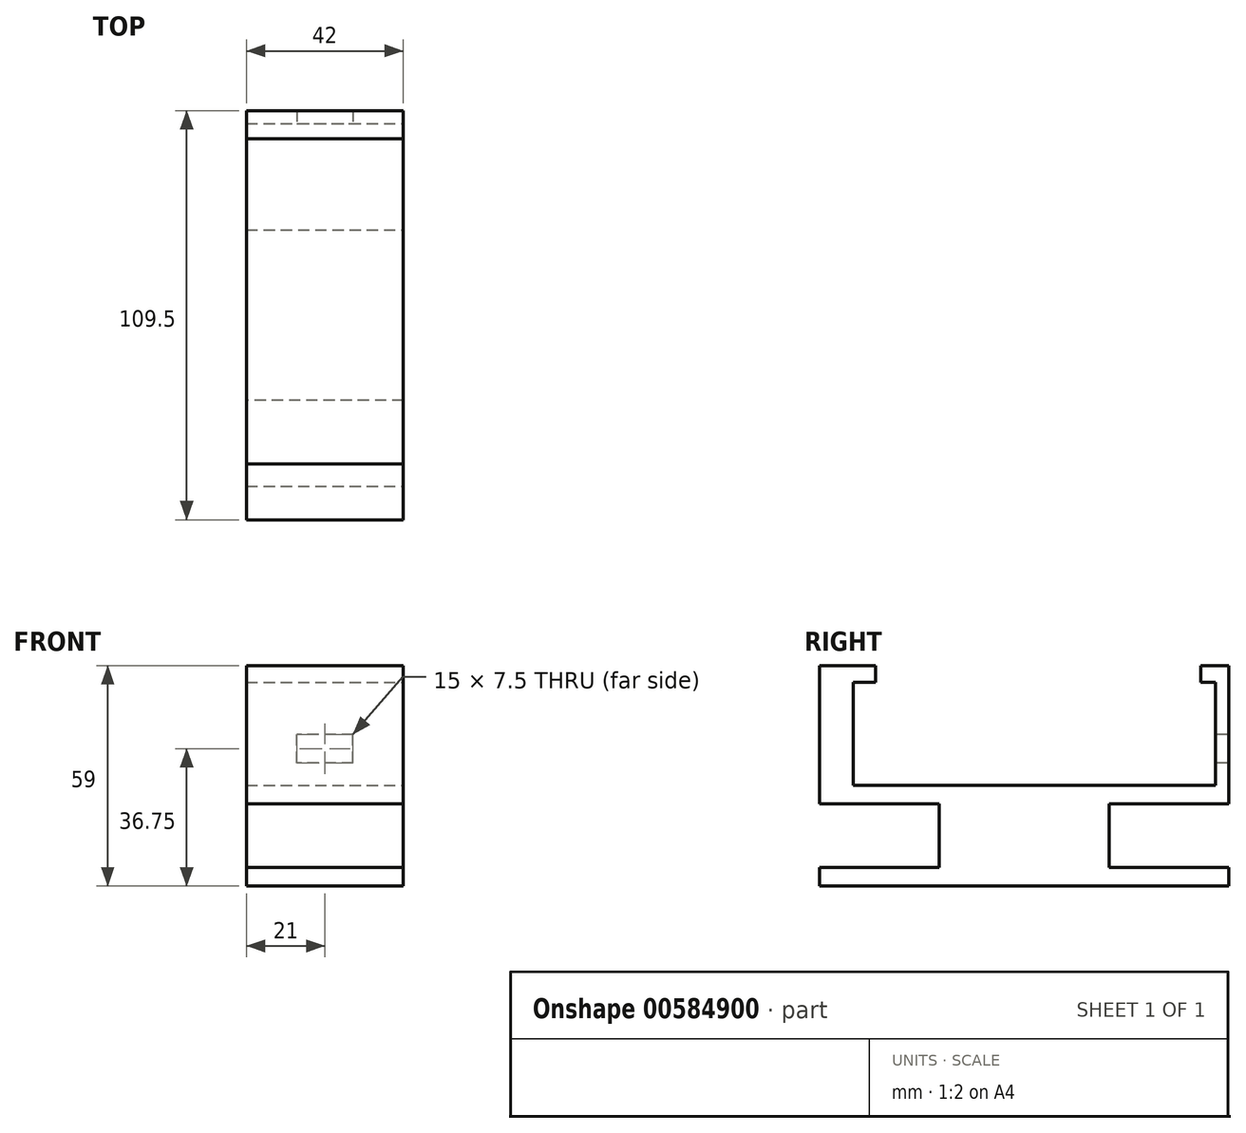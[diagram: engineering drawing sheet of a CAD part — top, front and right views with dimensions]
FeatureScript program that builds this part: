
annotation { "Feature Type Name" : "Feature", "Feature Type Description" : "" }
export const myFeature = defineFeature(function(context is Context, id is Id, definition is map)
    precondition{}
    {
        {
            var Q0;
            Q0=qCreatedBy(makeId("Top.planeOp"),FACE);
            var sketch = newSketch(context, id + "F0", { "sketchPlane" : qUnion([Q0])});
            skLineSegment(sketch, "E0.bottom", {"start": v(-21, 54.75) * mm, "end": v(21, 54.75) * mm});
            skLineSegment(sketch, "E0.top", {"start": v(-21, -54.75) * mm, "end": v(21, -54.75) * mm});
            skLineSegment(sketch, "E0.left", {"start": v(-21, 54.75) * mm, "end": v(-21, -54.75) * mm});
            skLineSegment(sketch, "E0.right", {"start": v(21, 54.75) * mm, "end": v(21, -54.75) * mm});
            skPoint(sketch, "E0.middle", {"position": v(0, 0) * mm});
            skSolve(sketch);
        }
        {
            var Q0;
            Q0=makeQuery(id+"F0.imprint","IMPRINT",FACE,{"disambiguationData":[TD([[makeQuery(id+"F0.imprint","IMPRINT",EDGE,{"derivedFrom":sQuery(id+"F0.wireOp",EDGE,"E0.bottom")}),-1.0]])]});
            extrude(context, id + "F1", {"entities" : qUnion([Q0]), "depth" : 5 * mm, "offsetDistance" : 25 * mm});
        }
        {
            var Q0;
            Q0=makeQuery(id+"F1.opExtrude","CAP_FACE",FACE,{"disambiguationData":[OSD([sQuery(id+"F0.wireOp",EDGE,"E0.bottom"),sQuery(id+"F0.wireOp",EDGE,"E0.top"),sQuery(id+"F0.wireOp",EDGE,"E0.left"),sQuery(id+"F0.wireOp",EDGE,"E0.right")])],"isStart":false});
            var sketch = newSketch(context, id + "F2", { "sketchPlane" : qUnion([Q0])});
            skLineSegment(sketch, "E1.bottom", {"start": v(-21, 54.75) * mm, "end": v(21, 54.75) * mm});
            skLineSegment(sketch, "E1.top", {"start": v(-21, 47.25) * mm, "end": v(21, 47.25) * mm});
            skLineSegment(sketch, "E1.left", {"start": v(-21, 54.75) * mm, "end": v(-21, 47.25) * mm});
            skLineSegment(sketch, "E1.right", {"start": v(21, 54.75) * mm, "end": v(21, 47.25) * mm});
            skPoint(sketch, "E1.middle", {"position": v(0, 51) * mm});
            skLineSegment(sketch, "E2.bottom", {"start": v(-21, -39.75) * mm, "end": v(21, -39.75) * mm});
            skLineSegment(sketch, "E2.top", {"start": v(-21, -54.75) * mm, "end": v(21, -54.75) * mm});
            skLineSegment(sketch, "E2.left", {"start": v(-21, -39.75) * mm, "end": v(-21, -54.75) * mm});
            skLineSegment(sketch, "E2.right", {"start": v(21, -39.75) * mm, "end": v(21, -54.75) * mm});
            skPoint(sketch, "E2.middle", {"position": v(0, -47.25) * mm});
            skSolve(sketch);
        }
        {
            var Q0;
            Q0=makeQuery(id+"F2.imprint","IMPRINT",FACE,{"disambiguationData":[TD([[makeQuery(id+"F2.imprint","IMPRINT",EDGE,{"derivedFrom":sQuery(id+"F2.wireOp",EDGE,"gTRGSuqZ-lPxv-xSsv-gjWA-rCe4dbmy2frY.bottom")}),-1.0]])]});
            var Q1;
            Q1=makeQuery(id+"F2.imprint","IMPRINT",FACE,{"disambiguationData":[TD([[makeQuery(id+"F2.imprint","IMPRINT",EDGE,{"derivedFrom":sQuery(id+"F2.wireOp",EDGE,"5NfKlNX9-xNwy-tjNF-5iGd-XRvzVmTsgCSR.bottom")}),1.0]])]});
            var Q2;
            Q2=makeQuery(id+"F2.imprint","IMPRINT",FACE,{"disambiguationData":[TD([[makeQuery(id+"F2.imprint","IMPRINT",EDGE,{"derivedFrom":sQuery(id+"F2.wireOp",EDGE,"E1.bottom")}),-1.0]])]});
            var Q3;
            Q3=makeQuery(id+"F2.imprint","IMPRINT",FACE,{"disambiguationData":[TD([[makeQuery(id+"F2.imprint","IMPRINT",EDGE,{"derivedFrom":sQuery(id+"F2.wireOp",EDGE,"E2.bottom")}),-1.0]])]});
            extrude(context, id + "F3", {"entities" : qUnion([Q0, Q1, Q2, Q3]), "operationType" : NewBodyOperationType.ADD, "depth" : 32 * mm, "offsetDistance" : 25 * mm});
        }
        {
            var Q0;
            Q0=makeQuery(id+"F3.opExtrude","SWEPT_FACE",FACE,{"disambiguationData":[OSD([sQuery(id+"F2.wireOp",EDGE,"E1.top")])]});
            var sketch = newSketch(context, id + "F4", { "sketchPlane" : qUnion([Q0])});
            skLineSegment(sketch, "E3.bottom", {"start": v(-21, 32.5) * mm, "end": v(21, 32.5) * mm});
            skLineSegment(sketch, "E3.top", {"start": v(-21, 5) * mm, "end": v(21, 5) * mm});
            skLineSegment(sketch, "E3.left", {"start": v(-21, 32.5) * mm, "end": v(-21, 5) * mm});
            skLineSegment(sketch, "E3.right", {"start": v(21, 32.5) * mm, "end": v(21, 5) * mm});
            skSolve(sketch);
        }
        {
            var Q0;
            Q0=makeQuery(id+"F4.imprint","IMPRINT",FACE,{"disambiguationData":[TD([[makeQuery(id+"F4.imprint","IMPRINT",EDGE,{"derivedFrom":sQuery(id+"F4.wireOp",EDGE,"E3.bottom")}),-1.0]])]});
            extrude(context, id + "F5", {"entities" : qUnion([Q0]), "operationType" : NewBodyOperationType.REMOVE, "oppositeDirection" : true, "depth" : 4 * mm, "offsetDistance" : 25 * mm});
        }
        {
            var Q0;
            Q0=makeQuery(id+"F3.opExtrude","SWEPT_FACE",FACE,{"disambiguationData":[OSD([sQuery(id+"F2.wireOp",EDGE,"E2.bottom")])]});
            var sketch = newSketch(context, id + "F6", { "sketchPlane" : qUnion([Q0])});
            skLineSegment(sketch, "E4.bottom", {"start": v(-21, 32.5) * mm, "end": v(21, 32.5) * mm});
            skLineSegment(sketch, "E4.top", {"start": v(-21, 5) * mm, "end": v(21, 5) * mm});
            skLineSegment(sketch, "E4.left", {"start": v(-21, 32.5) * mm, "end": v(-21, 5) * mm});
            skLineSegment(sketch, "E4.right", {"start": v(21, 32.5) * mm, "end": v(21, 5) * mm});
            skSolve(sketch);
        }
        {
            var Q0;
            Q0=makeQuery(id+"F6.imprint","IMPRINT",FACE,{"disambiguationData":[TD([[makeQuery(id+"F6.imprint","IMPRINT",EDGE,{"derivedFrom":sQuery(id+"F6.wireOp",EDGE,"E4.bottom")}),-1.0]])]});
            extrude(context, id + "F7", {"entities" : qUnion([Q0]), "operationType" : NewBodyOperationType.REMOVE, "oppositeDirection" : true, "depth" : 6 * mm, "offsetDistance" : 25 * mm});
        }
        {
            var Q0;
            Q0=makeQuery(id+"F5.boolean.opBoolean","COPY",FACE,{"derivedFrom":makeQuery(id+"F5.opExtrude","CAP_FACE",FACE,{"disambiguationData":[OSD([sQuery(id+"F4.wireOp",EDGE,"E3.bottom"),sQuery(id+"F4.wireOp",EDGE,"E3.top"),sQuery(id+"F4.wireOp",EDGE,"E3.left"),sQuery(id+"F4.wireOp",EDGE,"E3.right")])],"isStart":false})});
            var sketch = newSketch(context, id + "F8", { "sketchPlane" : qUnion([Q0])});
            skLineSegment(sketch, "E5.bottom", {"start": v(-7.5, 18.5) * mm, "end": v(7.5, 18.5) * mm});
            skLineSegment(sketch, "E5.top", {"start": v(-7.5, 11) * mm, "end": v(7.5, 11) * mm});
            skLineSegment(sketch, "E5.left", {"start": v(-7.5, 18.5) * mm, "end": v(-7.5, 11) * mm});
            skLineSegment(sketch, "E5.right", {"start": v(7.5, 18.5) * mm, "end": v(7.5, 11) * mm});
            skPoint(sketch, "E5.middle", {"position": v(0, 14.75) * mm});
            skSolve(sketch);
        }
        {
            var Q0;
            Q0=makeQuery(id+"F8.imprint","IMPRINT",FACE,{"disambiguationData":[TD([[makeQuery(id+"F8.imprint","IMPRINT",EDGE,{"derivedFrom":sQuery(id+"F8.wireOp",EDGE,"E5.bottom")}),-1.0]])]});
            extrude(context, id + "F9", {"entities" : qUnion([Q0]), "operationType" : NewBodyOperationType.REMOVE, "endBound" : BoundingType.THROUGH_ALL, "oppositeDirection" : true, "depth" : 25 * mm, "offsetDistance" : 25 * mm});
        }
        {
            var Q0;
            Q0=makeQuery(id+"F1.opExtrude","CAP_FACE",FACE,{"disambiguationData":[OSD([sQuery(id+"F0.wireOp",EDGE,"E0.bottom"),sQuery(id+"F0.wireOp",EDGE,"E0.top"),sQuery(id+"F0.wireOp",EDGE,"E0.left"),sQuery(id+"F0.wireOp",EDGE,"E0.right")])],"isStart":true});
            var sketch = newSketch(context, id + "F10", { "sketchPlane" : qUnion([Q0])});
            skLineSegment(sketch, "E6.bottom", {"start": v(-21, -54.75) * mm, "end": v(21, -54.75) * mm});
            skLineSegment(sketch, "E6.top", {"start": v(-21, 0) * mm, "end": v(21, 0) * mm});
            skLineSegment(sketch, "E6.left", {"start": v(-21, -54.75) * mm, "end": v(-21, 0) * mm});
            skLineSegment(sketch, "E6.right", {"start": v(21, -54.75) * mm, "end": v(21, 0) * mm});
            skLineSegment(sketch, "E7.bottom", {"start": v(-21, 54.75) * mm, "end": v(21, 54.75) * mm});
            skLineSegment(sketch, "E7.left", {"start": v(-21, 54.75) * mm, "end": v(-21, 0) * mm});
            skLineSegment(sketch, "E7.right", {"start": v(21, 54.75) * mm, "end": v(21, 0) * mm});
            skSolve(sketch);
        }
        {
            var Q0;
            Q0=qSketchRegion(id+"F10",true);
            extrude(context, id + "F11", {"entities" : qUnion([Q0]), "operationType" : NewBodyOperationType.ADD, "depth" : 22 * mm, "offsetDistance" : 25 * mm});
        }
        {
            var Q0;
            Q0=makeQuery(id+"F11.boolean.opBoolean","MERGE",FACE,{"derivedFrom":[makeQuery(id+"F3.boolean.opBoolean","MERGE",FACE,{"derivedFrom":[makeQuery(id+"F1.opExtrude","SWEPT_FACE",FACE,{"disambiguationData":[OSD([sQuery(id+"F0.wireOp",EDGE,"E0.bottom")])]}),makeQuery(id+"F3.opExtrude","SWEPT_FACE",FACE,{"disambiguationData":[OSD([sQuery(id+"F2.wireOp",EDGE,"E1.bottom")])]})]}),makeQuery(id+"F11.opExtrude","SWEPT_FACE",FACE,{"disambiguationData":[OSD([sQuery(id+"F10.wireOp",EDGE,"E6.bottom")])]})]});
            var sketch = newSketch(context, id + "F12", { "sketchPlane" : qUnion([Q0])});
            skLineSegment(sketch, "E8.bottom", {"start": v(21, -17) * mm, "end": v(-21, -17) * mm});
            skLineSegment(sketch, "E8.top", {"start": v(21, 0) * mm, "end": v(-21, 0) * mm});
            skLineSegment(sketch, "E8.left", {"start": v(21, -17) * mm, "end": v(21, 0) * mm});
            skLineSegment(sketch, "E8.right", {"start": v(-21, -17) * mm, "end": v(-21, 0) * mm});
            skSolve(sketch);
        }
        {
            var Q0;
            Q0=makeQuery(id+"F12.imprint","IMPRINT",FACE,{"disambiguationData":[TD([[makeQuery(id+"F12.imprint","IMPRINT",EDGE,{"derivedFrom":sQuery(id+"F12.wireOp",EDGE,"E8.bottom")}),-1.0]])]});
            extrude(context, id + "F13", {"entities" : qUnion([Q0]), "operationType" : NewBodyOperationType.REMOVE, "oppositeDirection" : true, "depth" : 32 * mm, "offsetDistance" : 25 * mm});
        }
        {
            var Q0;
            Q0=makeQuery(id+"F11.boolean.opBoolean","MERGE",FACE,{"derivedFrom":[makeQuery(id+"F3.boolean.opBoolean","MERGE",FACE,{"derivedFrom":[makeQuery(id+"F1.opExtrude","SWEPT_FACE",FACE,{"disambiguationData":[OSD([sQuery(id+"F0.wireOp",EDGE,"E0.top")])]}),makeQuery(id+"F3.opExtrude","SWEPT_FACE",FACE,{"disambiguationData":[OSD([sQuery(id+"F2.wireOp",EDGE,"E2.top")])]})]}),makeQuery(id+"F11.opExtrude","SWEPT_FACE",FACE,{"disambiguationData":[OSD([sQuery(id+"F10.wireOp",EDGE,"E7.bottom")])]})]});
            var sketch = newSketch(context, id + "F14", { "sketchPlane" : qUnion([Q0])});
            skLineSegment(sketch, "E9.bottom", {"start": v(21, -17) * mm, "end": v(-21, -17) * mm});
            skLineSegment(sketch, "E9.top", {"start": v(21, 0) * mm, "end": v(-21, 0) * mm});
            skLineSegment(sketch, "E9.left", {"start": v(21, -17) * mm, "end": v(21, 0) * mm});
            skLineSegment(sketch, "E9.right", {"start": v(-21, -17) * mm, "end": v(-21, 0) * mm});
            skSolve(sketch);
        }
        {
            var Q0;
            Q0=makeQuery(id+"F14.imprint","IMPRINT",FACE,{"disambiguationData":[TD([[makeQuery(id+"F14.imprint","IMPRINT",EDGE,{"derivedFrom":sQuery(id+"F14.wireOp",EDGE,"E9.bottom")}),-1.0]])]});
            extrude(context, id + "F15", {"entities" : qUnion([Q0]), "operationType" : NewBodyOperationType.REMOVE, "oppositeDirection" : true, "depth" : 32 * mm, "offsetDistance" : 25 * mm});
        }
    });
